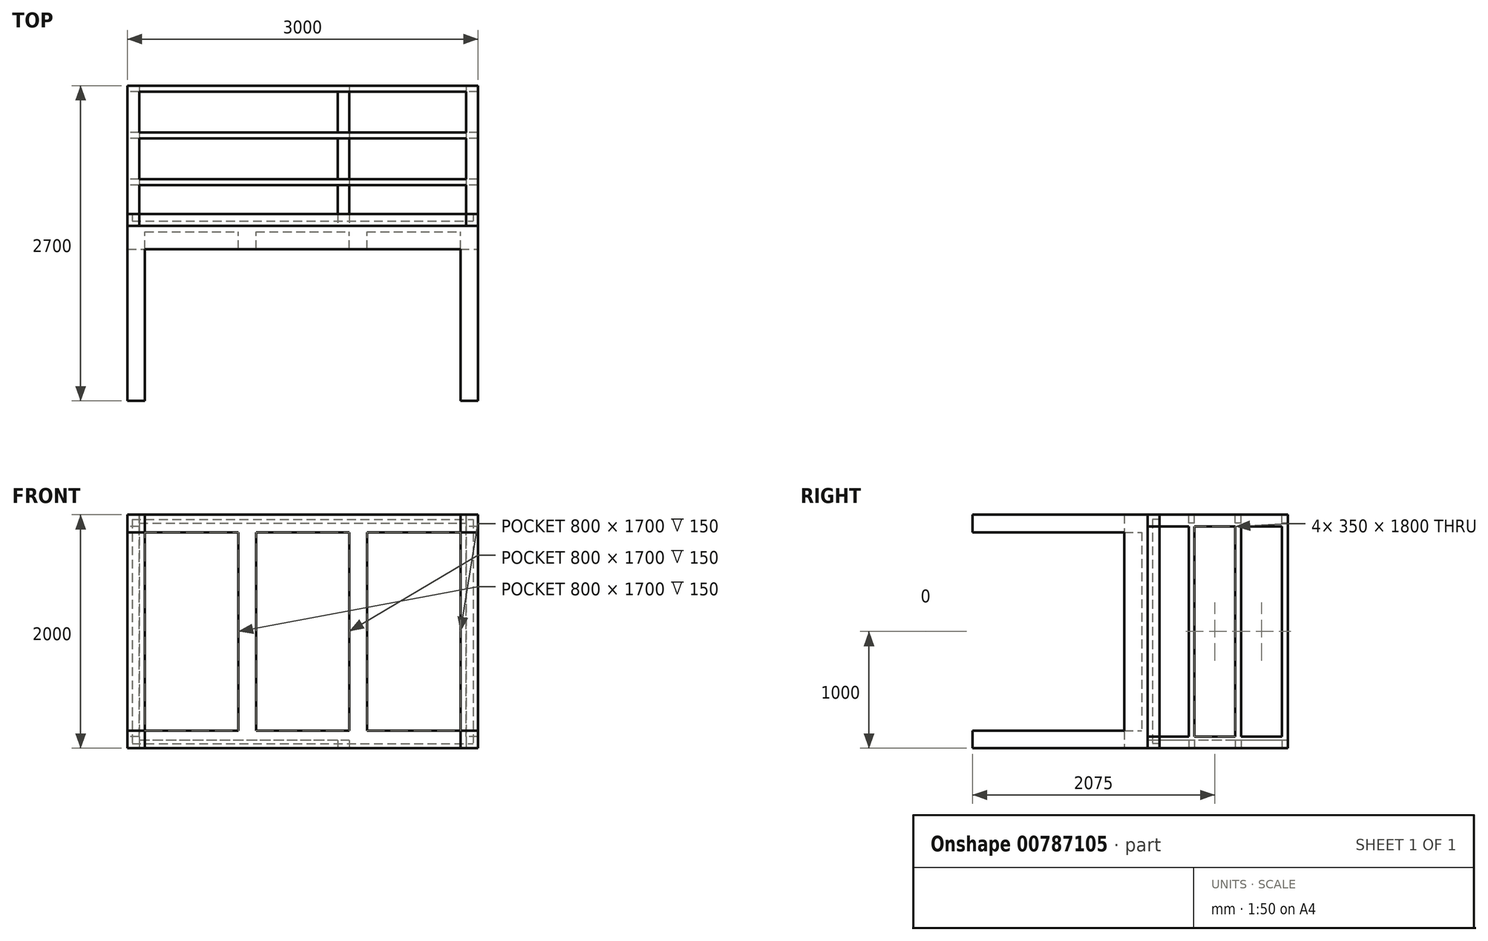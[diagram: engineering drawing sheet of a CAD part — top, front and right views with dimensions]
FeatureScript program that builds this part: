
annotation { "Feature Type Name" : "Feature", "Feature Type Description" : "" }
export const myFeature = defineFeature(function(context is Context, id is Id, definition is map)
    precondition{}
    {
        {
            var Q0;
            Q0=qCreatedBy(makeId("Front.planeOp"),FACE);
            var sketch = newSketch(context, id + "F0", { "sketchPlane" : qUnion([Q0])});
            skLineSegment(sketch, "E0.bottom", {"start": v(-1500, 1000) * mm, "end": v(1500, 1000) * mm});
            skLineSegment(sketch, "E0.top", {"start": v(-1500, -1000) * mm, "end": v(1500, -1000) * mm});
            skLineSegment(sketch, "E0.left", {"start": v(-1500, 1000) * mm, "end": v(-1500, -1000) * mm});
            skLineSegment(sketch, "E0.right", {"start": v(1500, 1000) * mm, "end": v(1500, -1000) * mm});
            skPoint(sketch, "E0.middle", {"position": v(0, 0) * mm});
            skSolve(sketch);
        }
        {
            var Q0;
            Q0 = qSketchRegion(id + "F0", true);
            extrude(context, id + "F1", {"entities" : qUnion([Q0]), "depth" : 50 * mm, "offsetDistance" : 25 * mm});
        }
        {
            var Q0;
            Q0=makeQuery(id+"F1.opExtrude","CAP_FACE",FACE,{"disambiguationData":[OSD([sQuery(id+"F0.wireOp",EDGE,"E0.bottom"),sQuery(id+"F0.wireOp",EDGE,"E0.top"),sQuery(id+"F0.wireOp",EDGE,"E0.left"),sQuery(id+"F0.wireOp",EDGE,"E0.right")])],"isStart":false});
            var sketch = newSketch(context, id + "F2", { "sketchPlane" : qUnion([Q0])});
            skLineSegment(sketch, "E1.bottom", {"start": v(-1500, 1000) * mm, "end": v(-1350, 1000) * mm});
            skLineSegment(sketch, "E1.top", {"start": v(-1500, 850) * mm, "end": v(-1350, 850) * mm});
            skLineSegment(sketch, "E1.left", {"start": v(-1500, 1000) * mm, "end": v(-1500, 850) * mm});
            skLineSegment(sketch, "E1.right", {"start": v(-1350, 1000) * mm, "end": v(-1350, 850) * mm});
            skLineSegment(sketch, "E2.bottom", {"start": v(1350, 1000) * mm, "end": v(1500, 1000) * mm});
            skLineSegment(sketch, "E2.top", {"start": v(1350, 850) * mm, "end": v(1500, 850) * mm});
            skLineSegment(sketch, "E2.left", {"start": v(1350, 1000) * mm, "end": v(1350, 850) * mm});
            skLineSegment(sketch, "E2.right", {"start": v(1500, 1000) * mm, "end": v(1500, 850) * mm});
            skLineSegment(sketch, "E3.bottom", {"start": v(-1500, -850) * mm, "end": v(-1350, -850) * mm});
            skLineSegment(sketch, "E3.top", {"start": v(-1500, -1000) * mm, "end": v(-1350, -1000) * mm});
            skLineSegment(sketch, "E3.left", {"start": v(-1500, -850) * mm, "end": v(-1500, -1000) * mm});
            skLineSegment(sketch, "E3.right", {"start": v(-1350, -850) * mm, "end": v(-1350, -1000) * mm});
            skLineSegment(sketch, "E4.bottom", {"start": v(1500, -850) * mm, "end": v(1350, -850) * mm});
            skLineSegment(sketch, "E4.top", {"start": v(1500, -1000) * mm, "end": v(1350, -1000) * mm});
            skLineSegment(sketch, "E4.left", {"start": v(1500, -850) * mm, "end": v(1500, -1000) * mm});
            skLineSegment(sketch, "E4.right", {"start": v(1350, -850) * mm, "end": v(1350, -1000) * mm});
            skSolve(sketch);
        }
        {
            var Q0;
            Q0 = qSketchRegion(id + "F2", true);
            extrude(context, id + "F3", {"entities" : qUnion([Q0]), "operationType" : NewBodyOperationType.ADD, "depth" : 1450 * mm, "offsetDistance" : 25 * mm});
        }
        {
            var Q0;
            Q0=makeQuery(id+"F1.opExtrude","CAP_FACE",FACE,{"disambiguationData":[OSD([sQuery(id+"F0.wireOp",EDGE,"E0.bottom"),sQuery(id+"F0.wireOp",EDGE,"E0.top"),sQuery(id+"F0.wireOp",EDGE,"E0.left"),sQuery(id+"F0.wireOp",EDGE,"E0.right")])],"isStart":true});
            var sketch = newSketch(context, id + "F4", { "sketchPlane" : qUnion([Q0])});
            skLineSegment(sketch, "E5", {"start": v(-1400, 927.5) * mm, "end": v(1400, 927.5) * mm});
            skLineSegment(sketch, "E6", {"start": v(-1400, 927.5) * mm, "end": v(-1400, -1000) * mm});
            skLineSegment(sketch, "E7", {"start": v(1400, 927.5) * mm, "end": v(1400, -933.33) * mm});
            skLineSegment(sketch, "E8", {"start": v(-400, -933.33) * mm, "end": v(-400, -1000) * mm});
            skLineSegment(sketch, "E9", {"start": v(-400, -933.33) * mm, "end": v(1400, -933.33) * mm});
            skPoint(sketch, "E10.orphan", {"position": v(1400, -1000) * mm});
            skSolve(sketch);
        }
        {
            var Q0;
            Q0 = qSketchRegion(id + "F4", true);
            var Q1;
            Q1=makeQuery(id+"F4.imprint","IMPRINT",FACE,{"disambiguationData":[TD([[makeQuery(id+"F4.imprint","IMPRINT",EDGE,{"derivedFrom":sQuery(id+"F4.wireOp",EDGE,"E5")}),1.0]])]});
            extrude(context, id + "F5", {"entities" : qUnion([Q0, Q1]), "depth" : 1200 * mm, "offsetDistance" : 25 * mm});
        }
        {
            var Q0;
            Q0=makeQuery(id+"F5.opExtrude","SWEPT_FACE",FACE,{"disambiguationData":[OSD([sQuery(id+"F0.wireOp",EDGE,"E0.left")])]});
            var sketch = newSketch(context, id + "F6", { "sketchPlane" : qUnion([Q0])});
            skLineSegment(sketch, "E11", {"start": v(-1150, -900) * mm, "end": v(-1150, 900) * mm});
            skLineSegment(sketch, "E12", {"start": v(-800, -900) * mm, "end": v(-800, 900) * mm});
            skLineSegment(sketch, "E13", {"start": v(-750, -900) * mm, "end": v(-750, 900) * mm});
            skLineSegment(sketch, "E14", {"start": v(-400, -900) * mm, "end": v(-400, 900) * mm});
            skLineSegment(sketch, "E15", {"start": v(-350, -900) * mm, "end": v(-350, 900) * mm});
            skLineSegment(sketch, "E16", {"start": v(-1150, -900) * mm, "end": v(-800, -900) * mm});
            skLineSegment(sketch, "E17", {"start": v(-1150, 900) * mm, "end": v(-800, 900) * mm});
            skLineSegment(sketch, "E18.trimOffspring", {"start": v(-750, 900) * mm, "end": v(-400, 900) * mm});
            skLineSegment(sketch, "E19.trimOffspring", {"start": v(-350, 900) * mm, "end": v(0, 900) * mm});
            skLineSegment(sketch, "E20.trimOffspring", {"start": v(-350, -900) * mm, "end": v(0, -900) * mm});
            skLineSegment(sketch, "E21.trimOffspring", {"start": v(-750, -900) * mm, "end": v(-400, -900) * mm});
            skSolve(sketch);
        }
        {
            var Q0;
            Q0=makeQuery(id+"F6.imprint","IMPRINT",FACE,{"disambiguationData":[TD([[makeQuery(id+"F6.imprint","IMPRINT",EDGE,{"derivedFrom":sQuery(id+"F6.wireOp",EDGE,"E11")}),-1.0]])]});
            var Q1;
            Q1=makeQuery(id+"F6.imprint","IMPRINT",FACE,{"disambiguationData":[TD([[makeQuery(id+"F6.imprint","IMPRINT",EDGE,{"derivedFrom":sQuery(id+"F6.wireOp",EDGE,"E13")}),-1.0]])]});
            var Q2;
            Q2=makeQuery(id+"F6.imprint","IMPRINT",FACE,{"disambiguationData":[TD([[makeQuery(id+"F6.imprint","IMPRINT",EDGE,{"derivedFrom":sQuery(id+"F6.wireOp",EDGE,"E15")}),-1.0]])]});
            extrude(context, id + "F7", {"entities" : qUnion([Q0, Q1, Q2]), "operationType" : NewBodyOperationType.REMOVE, "endBound" : BoundingType.THROUGH_ALL, "oppositeDirection" : true, "depth" : 25 * mm, "offsetDistance" : 25 * mm});
        }
        {
            var Q0;
            {var subQ0=sQuery(id+"F0.wireOp",EDGE,"E0.top");var subQ1=makeQuery(id+"F1.opExtrude","CAP_EDGE",EDGE,{"disambiguationData":[OSD([subQ0])],"isStart":true});Q0=makeQuery(id+"F5.opExtrude","SWEPT_FACE",FACE,{"disambiguationData":[OSD([subQ0]),TDD([makeQuery(id+"F4.imprint","IMPRINT",EDGE,{"disambiguationData":[TD([[makeQuery(id+"F4.imprint","INTERSECT",VERTEX,{"derivedFrom":[subQ1,makeQuery(id+"F1.opExtrude","CAP_EDGE",EDGE,{"disambiguationData":[OSD([sQuery(id+"F0.wireOp",EDGE,"E0.left")])],"isStart":true})]}),-1.0]])],"derivedFrom":subQ1})])]});}
            var sketch = newSketch(context, id + "F8", { "sketchPlane" : qUnion([Q0])});
            skLineSegment(sketch, "E22", {"start": v(300, 0) * mm, "end": v(300, -350) * mm});
            skLineSegment(sketch, "E23", {"start": v(-1400, -350) * mm, "end": v(300, -350) * mm});
            skLineSegment(sketch, "E24", {"start": v(-1400, -400) * mm, "end": v(300, -400) * mm});
            skLineSegment(sketch, "E25", {"start": v(-1400, -750) * mm, "end": v(300, -750) * mm});
            skLineSegment(sketch, "E26", {"start": v(-1400, -800) * mm, "end": v(300, -800) * mm});
            skLineSegment(sketch, "E27", {"start": v(-1400, -1150) * mm, "end": v(300, -1150) * mm});
            skLineSegment(sketch, "E28.trimOffspring", {"start": v(300, -400) * mm, "end": v(300, -750) * mm});
            skLineSegment(sketch, "E29.trimOffspring", {"start": v(300, -800) * mm, "end": v(300, -1150) * mm});
            skLineSegment(sketch, "E30", {"start": v(-1400, 0) * mm, "end": v(-1400, -350) * mm});
            skLineSegment(sketch, "E31.trimOffspring", {"start": v(-1400, -400) * mm, "end": v(-1400, -750) * mm});
            skLineSegment(sketch, "E32.trimOffspring", {"start": v(-1400, -800) * mm, "end": v(-1400, -1150) * mm});
            skSolve(sketch);
        }
        {
            var Q0;
            Q0=makeQuery(id+"F8.imprint","IMPRINT",FACE,{"disambiguationData":[TD([[makeQuery(id+"F8.imprint","IMPRINT",EDGE,{"derivedFrom":sQuery(id+"F8.wireOp",EDGE,"E26")}),-1.0]])]});
            var Q1;
            {var subQ0=sQuery(id+"F8.wireOp",EDGE,"E22");Q1=makeQuery(id+"F8.imprint","IMPRINT",FACE,{"disambiguationData":[TD([[makeQuery(id+"F8.imprint","IMPRINT",EDGE,{"derivedFrom":subQ0}),-1.0]])]});}
            var Q2;
            Q2=makeQuery(id+"F8.imprint","IMPRINT",FACE,{"disambiguationData":[TD([[makeQuery(id+"F8.imprint","IMPRINT",EDGE,{"derivedFrom":sQuery(id+"F8.wireOp",EDGE,"E24")}),-1.0]])]});
            extrude(context, id + "F9", {"entities" : qUnion([Q0, Q1, Q2]), "operationType" : NewBodyOperationType.REMOVE, "oppositeDirection" : true, "depth" : 110 * mm, "offsetDistance" : 25 * mm});
        }
        {
            var Q0;
            Q0=makeQuery(id+"F5.opExtrude","SWEPT_FACE",FACE,{"disambiguationData":[OSD([sQuery(id+"F0.wireOp",EDGE,"E0.bottom")])]});
            var sketch = newSketch(context, id + "F10", { "sketchPlane" : qUnion([Q0])});
            skLineSegment(sketch, "E33", {"start": v(-1400, 1150) * mm, "end": v(-1400, 800) * mm});
            skLineSegment(sketch, "E34", {"start": v(1400, 1150) * mm, "end": v(1400, 800) * mm});
            skLineSegment(sketch, "E35", {"start": v(-1400, 1150) * mm, "end": v(1400, 1150) * mm});
            skLineSegment(sketch, "E36", {"start": v(-1400, 800) * mm, "end": v(1400, 800) * mm});
            skLineSegment(sketch, "E37", {"start": v(-1400, 750) * mm, "end": v(1400, 750) * mm});
            skLineSegment(sketch, "E38", {"start": v(-1400, 400) * mm, "end": v(1400, 400) * mm});
            skLineSegment(sketch, "E39", {"start": v(1400, 350) * mm, "end": v(-1400, 350) * mm});
            skLineSegment(sketch, "E40.trimOffspring", {"start": v(1400, 750) * mm, "end": v(1400, 400) * mm});
            skLineSegment(sketch, "E41.trimOffspring", {"start": v(1400, 350) * mm, "end": v(1400, 0) * mm});
            skLineSegment(sketch, "E42.trimOffspring", {"start": v(-1400, 350) * mm, "end": v(-1400, 0) * mm});
            skLineSegment(sketch, "E43.trimOffspring", {"start": v(-1400, 750) * mm, "end": v(-1400, 400) * mm});
            skSolve(sketch);
        }
        {
            var Q0;
            Q0=makeQuery(id+"F10.imprint","IMPRINT",FACE,{"disambiguationData":[TD([[makeQuery(id+"F10.imprint","IMPRINT",EDGE,{"derivedFrom":sQuery(id+"F10.wireOp",EDGE,"E33")}),1.0]])]});
            var Q1;
            Q1=makeQuery(id+"F10.imprint","IMPRINT",FACE,{"disambiguationData":[TD([[makeQuery(id+"F10.imprint","IMPRINT",EDGE,{"derivedFrom":sQuery(id+"F10.wireOp",EDGE,"E37")}),-1.0]])]});
            var Q2;
            Q2=makeQuery(id+"F10.imprint","IMPRINT",FACE,{"disambiguationData":[TD([[makeQuery(id+"F10.imprint","IMPRINT",EDGE,{"derivedFrom":sQuery(id+"F10.wireOp",EDGE,"E39")}),1.0]])]});
            extrude(context, id + "F11", {"entities" : qUnion([Q0, Q1, Q2]), "operationType" : NewBodyOperationType.REMOVE, "oppositeDirection" : true, "depth" : 110 * mm, "offsetDistance" : 25 * mm});
        }
        {
            var Q0;
            Q0=makeQuery(id+"F1.opExtrude","CAP_FACE",FACE,{"disambiguationData":[OSD([sQuery(id+"F0.wireOp",EDGE,"E0.bottom"),sQuery(id+"F0.wireOp",EDGE,"E0.top"),sQuery(id+"F0.wireOp",EDGE,"E0.left"),sQuery(id+"F0.wireOp",EDGE,"E0.right")])],"isStart":true});
            extrude(context, id + "F12", {"entities" : qUnion([Q0]), "depth" : 100 * mm, "offsetDistance" : 25 * mm});
        }
        {
            var Q0;
            Q0=makeQuery(id+"F1.opExtrude","CAP_FACE",FACE,{"disambiguationData":[OSD([sQuery(id+"F0.wireOp",EDGE,"E0.bottom"),sQuery(id+"F0.wireOp",EDGE,"E0.top"),sQuery(id+"F0.wireOp",EDGE,"E0.left"),sQuery(id+"F0.wireOp",EDGE,"E0.right")])],"isStart":false});
            var sketch = newSketch(context, id + "F13", { "sketchPlane" : qUnion([Q0])});
            skLineSegment(sketch, "E44", {"start": v(-1350, 850) * mm, "end": v(-1350, -850) * mm});
            skLineSegment(sketch, "E45", {"start": v(1350, 850) * mm, "end": v(1350, -850) * mm});
            skLineSegment(sketch, "E46", {"start": v(-1350, 850) * mm, "end": v(1350, 850) * mm});
            skLineSegment(sketch, "E47", {"start": v(-1350, -850) * mm, "end": v(1350, -850) * mm});
            skSolve(sketch);
        }
        {
            var Q0;
            Q0=makeQuery(id+"F13.imprint","IMPRINT",FACE,{"disambiguationData":[TD([[makeQuery(id+"F13.imprint","IMPRINT",EDGE,{"derivedFrom":sQuery(id+"F13.wireOp",EDGE,"E44")}),-1.0]])]});
            var Q1;
            Q1=makeQuery(id+"F13.imprint","IMPRINT",FACE,{"disambiguationData":[TD([[makeQuery(id+"F13.imprint","IMPRINT",EDGE,{"derivedFrom":sQuery(id+"F13.wireOp",EDGE,"E46")}),1.0]])]});
            var Q2;
            Q2=makeQuery(id+"F13.imprint","IMPRINT",FACE,{"disambiguationData":[TD([[makeQuery(id+"F13.imprint","IMPRINT",EDGE,{"derivedFrom":sQuery(id+"F13.wireOp",EDGE,"E45")}),1.0]])]});
            var Q3;
            Q3=makeQuery(id+"F13.imprint","IMPRINT",FACE,{"disambiguationData":[TD([[makeQuery(id+"F13.imprint","IMPRINT",EDGE,{"derivedFrom":sQuery(id+"F13.wireOp",EDGE,"E47")}),-1.0]])]});
            extrude(context, id + "F14", {"entities" : qUnion([Q0, Q1, Q2, Q3]), "operationType" : NewBodyOperationType.ADD, "depth" : 150 * mm, "offsetDistance" : 25 * mm});
        }
        {
            var Q0;
            Q0=makeQuery(id+"F1.opExtrude","CAP_FACE",FACE,{"disambiguationData":[OSD([sQuery(id+"F0.wireOp",EDGE,"E0.bottom"),sQuery(id+"F0.wireOp",EDGE,"E0.top"),sQuery(id+"F0.wireOp",EDGE,"E0.left"),sQuery(id+"F0.wireOp",EDGE,"E0.right")])],"isStart":false});
            var sketch = newSketch(context, id + "F15", { "sketchPlane" : qUnion([Q0])});
            skLineSegment(sketch, "E48.bottom", {"start": v(-550, 850) * mm, "end": v(-400, 850) * mm});
            skLineSegment(sketch, "E48.top", {"start": v(-550, -850) * mm, "end": v(-400, -850) * mm});
            skLineSegment(sketch, "E48.left", {"start": v(-550, 850) * mm, "end": v(-550, -850) * mm});
            skLineSegment(sketch, "E48.right", {"start": v(-400, 850) * mm, "end": v(-400, -850) * mm});
            skLineSegment(sketch, "E49.bottom", {"start": v(400, 850) * mm, "end": v(550, 850) * mm});
            skLineSegment(sketch, "E49.top", {"start": v(400, -850) * mm, "end": v(550, -850) * mm});
            skLineSegment(sketch, "E49.left", {"start": v(400, 850) * mm, "end": v(400, -850) * mm});
            skLineSegment(sketch, "E49.right", {"start": v(550, 850) * mm, "end": v(550, -850) * mm});
            skSolve(sketch);
        }
        {
            var Q0;
            Q0=makeQuery(id+"F15.imprint","IMPRINT",FACE,{"disambiguationData":[TD([[makeQuery(id+"F15.imprint","IMPRINT",EDGE,{"derivedFrom":sQuery(id+"F15.wireOp",EDGE,"E48.bottom")}),-1.0]])]});
            var Q1;
            Q1=makeQuery(id+"F15.imprint","IMPRINT",FACE,{"disambiguationData":[TD([[makeQuery(id+"F15.imprint","IMPRINT",EDGE,{"derivedFrom":sQuery(id+"F15.wireOp",EDGE,"E49.bottom")}),-1.0]])]});
            extrude(context, id + "F16", {"entities" : qUnion([Q0, Q1]), "operationType" : NewBodyOperationType.ADD, "depth" : 150 * mm, "offsetDistance" : 25 * mm});
        }
        {
            var Q0;
            Q0=makeQuery(id+"F12.opExtrude","CAP_FACE",FACE,{"disambiguationData":[OSD([sQuery(id+"F0.wireOp",EDGE,"E0.bottom"),sQuery(id+"F0.wireOp",EDGE,"E0.top"),sQuery(id+"F0.wireOp",EDGE,"E0.left"),sQuery(id+"F0.wireOp",EDGE,"E0.right")])],"isStart":false});
            shell(context, id + "F17", {"entities" : qUnion([Q0]), "thickness" : 40 * mm});
        }
    });
